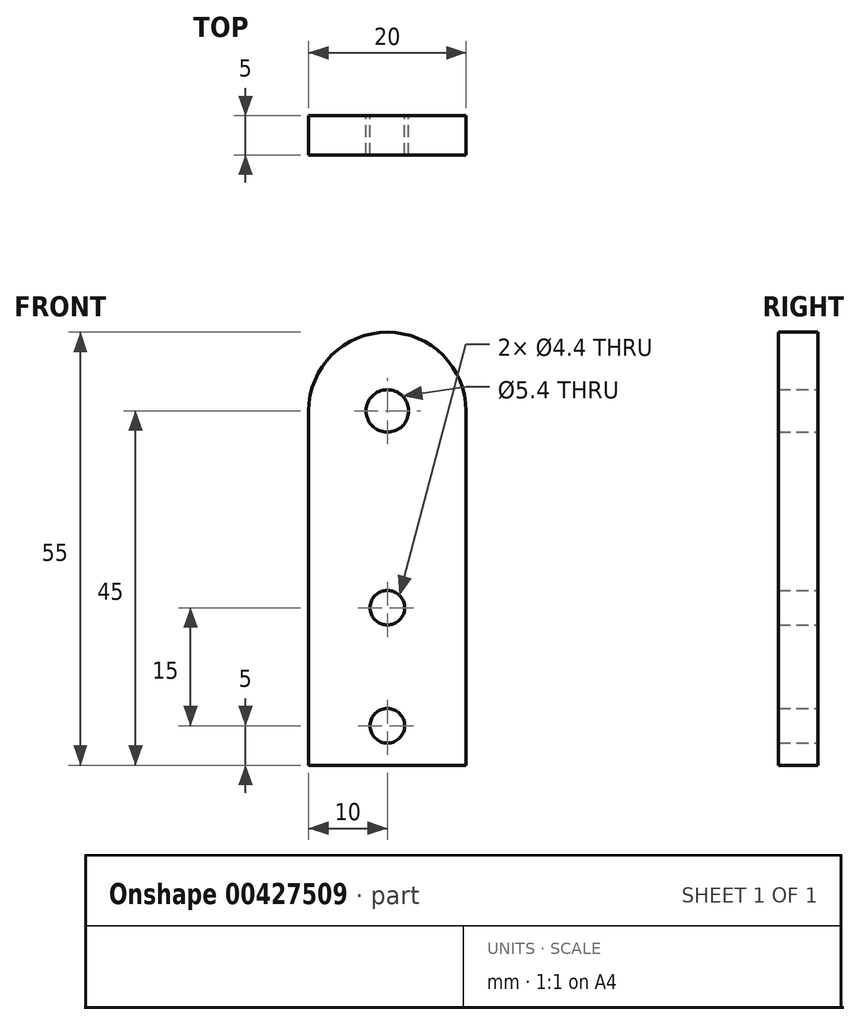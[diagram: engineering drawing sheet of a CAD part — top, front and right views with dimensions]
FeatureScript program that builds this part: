
annotation { "Feature Type Name" : "Feature", "Feature Type Description" : "" }
export const myFeature = defineFeature(function(context is Context, id is Id, definition is map)
    precondition{}
    {
        {
            var Q0;
            Q0=qCreatedBy(makeId("Front.planeOp"),FACE);
            var sketch = newSketch(context, id + "F0", { "sketchPlane" : qUnion([Q0])});
            skLineSegment(sketch, "E0", {"start": v(-10, -45) * mm, "end": v(10, -45) * mm});
            skLineSegment(sketch, "E1", {"start": v(10, -45) * mm, "end": v(10, 0) * mm});
            skLineSegment(sketch, "E2", {"start": v(-10, 0) * mm, "end": v(-10, -45) * mm});
            skCircle(sketch, "E3", {"center": v(0, -40) * mm, "radius": 2.2 * mm});
            skCircle(sketch, "E4", {"center": v(0, -25) * mm, "radius": 2.2 * mm});
            skCircle(sketch, "E5", {"center": v(0, 0) * mm, "radius": 2.7 * mm});
            skArc(sketch, "E6", {"start": v(10, 0) * mm, "mid": v(0, 10) * mm, "end": v(-10, 0) * mm});
            skSolve(sketch);
        }
        {
            var Q0;
            Q0=makeQuery(id+"F0.imprint","IMPRINT",FACE,{"disambiguationData":[TD([[makeQuery(id+"F0.imprint","IMPRINT",EDGE,{"derivedFrom":sQuery(id+"F0.wireOp",EDGE,"E0")}),1.0]])]});
            extrude(context, id + "F1", {"entities" : qUnion([Q0]), "depth" : 5 * mm});
        }
    });
